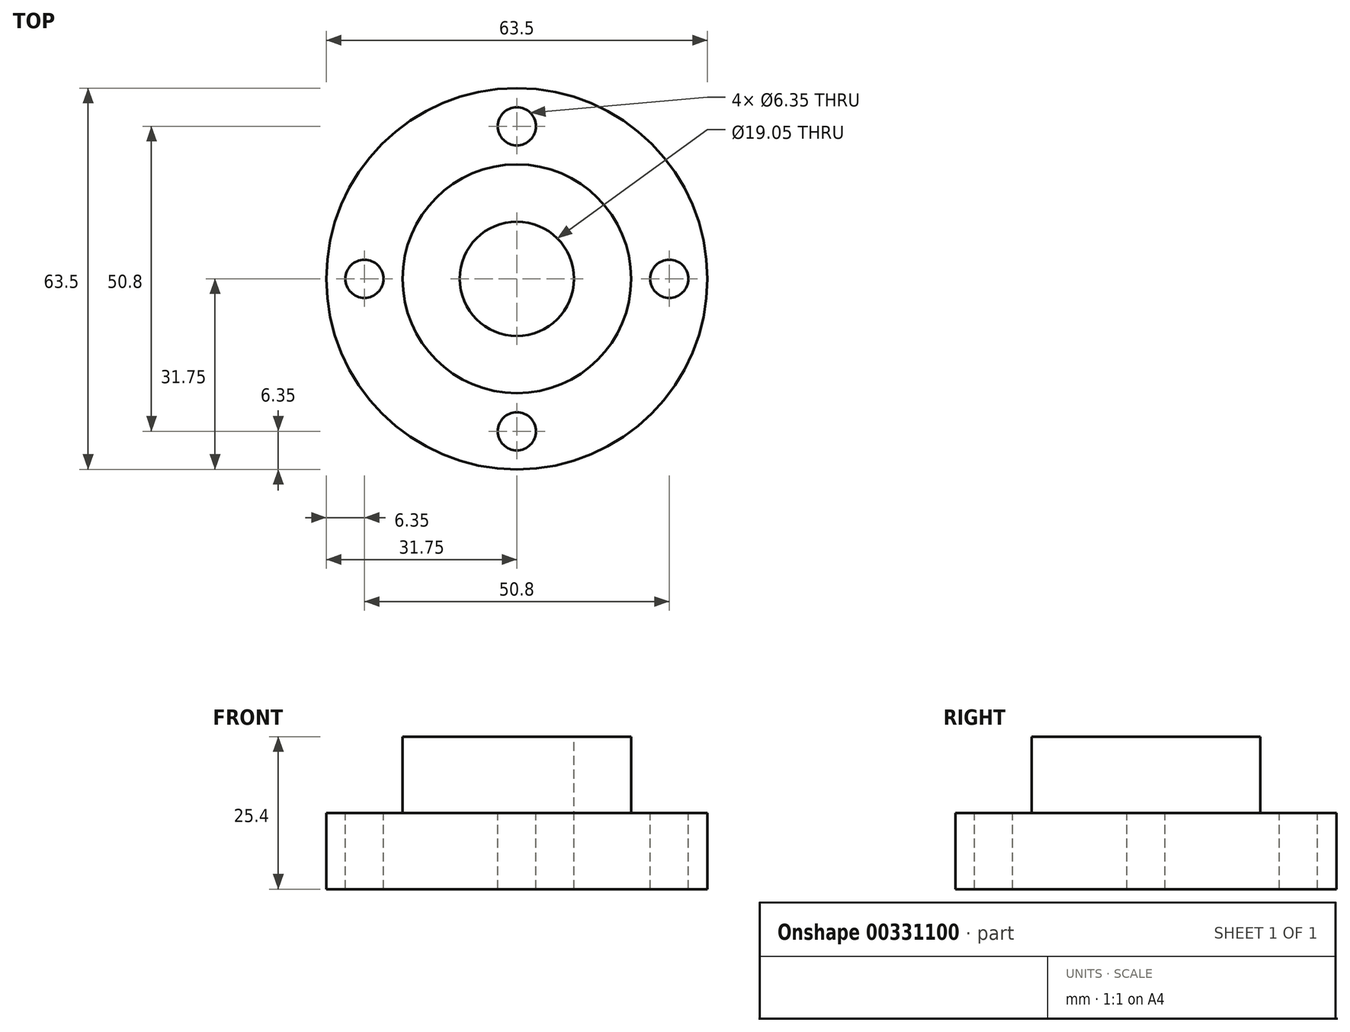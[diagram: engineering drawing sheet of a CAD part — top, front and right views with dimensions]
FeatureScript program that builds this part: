
annotation { "Feature Type Name" : "Feature", "Feature Type Description" : "" }
export const myFeature = defineFeature(function(context is Context, id is Id, definition is map)
    precondition{}
    {
        {
            var Q0;
            Q0=qCreatedBy(makeId("Top.planeOp"),FACE);
            var sketch = newSketch(context, id + "F0", { "sketchPlane" : qUnion([Q0])});
            skLineSegment(sketch, "E0", {"start": v(0, 0) * mm, "end": v(0, 63.5) * mm});
            skLineSegment(sketch, "E1", {"start": v(0, 63.5) * mm, "end": v(63.5, 63.5) * mm});
            skLineSegment(sketch, "E2", {"start": v(63.5, 63.5) * mm, "end": v(63.5, 0) * mm});
            skLineSegment(sketch, "E3", {"start": v(63.5, 0) * mm, "end": v(0, 0) * mm});
            skSolve(sketch);
        }
        {
            var Q0;
            Q0 = qSketchRegion(id + "F0", true);
            extrude(context, id + "F1", {"entities" : qUnion([Q0]), "depth" : 25.4 * mm});
        }
        {
            var Q0;
            Q0=makeQuery(id+"F1.opExtrude","CAP_FACE",FACE,{"disambiguationData":[OSD([sQuery(id+"F0.wireOp",EDGE,"E0"),sQuery(id+"F0.wireOp",EDGE,"E1"),sQuery(id+"F0.wireOp",EDGE,"E2"),sQuery(id+"F0.wireOp",EDGE,"E3")])],"isStart":false});
            var sketch = newSketch(context, id + "F2", { "sketchPlane" : qUnion([Q0])});
            skLineSegment(sketch, "E4", {"start": v(0, 63.5) * mm, "end": v(63.5, 63.5) * mm});
            skLineSegment(sketch, "E5", {"start": v(63.5, 63.5) * mm, "end": v(63.5, 0) * mm});
            skLineSegment(sketch, "E6", {"start": v(63.5, 0) * mm, "end": v(0, 0) * mm});
            skLineSegment(sketch, "E7", {"start": v(0, 0) * mm, "end": v(0, 63.5) * mm});
            skLineSegment(sketch, "E8", {"start": v(31.75, 50.8) * mm, "end": v(50.8, 50.8) * mm});
            skLineSegment(sketch, "E9", {"start": v(50.8, 50.8) * mm, "end": v(50.8, 31.75) * mm});
            skLineSegment(sketch, "E10", {"start": v(50.8, 31.75) * mm, "end": v(50.8, 12.7) * mm});
            skLineSegment(sketch, "E11", {"start": v(50.8, 12.7) * mm, "end": v(12.7, 12.7) * mm});
            skLineSegment(sketch, "E12", {"start": v(12.7, 12.7) * mm, "end": v(12.7, 50.8) * mm});
            skLineSegment(sketch, "E13", {"start": v(12.7, 50.8) * mm, "end": v(31.75, 50.8) * mm});
            skPoint(sketch, "E14.orphan", {"position": v(31.75, 31.75) * mm});
            skPoint(sketch, "E15.start.orphan", {"position": v(0, 31.75) * mm});
            skPoint(sketch, "E16.trimOffspring.end.orphan", {"position": v(63.5, 31.75) * mm});
            skSolve(sketch);
        }
        {
            var Q0;
            Q0=makeQuery(id+"F2.imprint","IMPRINT",FACE,{"disambiguationData":[TD([[makeQuery(id+"F2.imprint","IMPRINT",EDGE,{"derivedFrom":sQuery(id+"F2.wireOp",EDGE,"E4")}),-1.0]])]});
            extrude(context, id + "F3", {"entities" : qUnion([Q0]), "operationType" : NewBodyOperationType.REMOVE, "oppositeDirection" : true, "depth" : 12.7 * mm});
        }
        {
            var Q0;
            Q0=makeQuery(id+"F3.boolean.opBoolean","COPY",FACE,{"derivedFrom":makeQuery(id+"F3.opExtrude","CAP_FACE",FACE,{"disambiguationData":[OSD([sQuery(id+"F2.wireOp",EDGE,"E4"),sQuery(id+"F2.wireOp",EDGE,"E5"),sQuery(id+"F2.wireOp",EDGE,"E6"),sQuery(id+"F2.wireOp",EDGE,"E7"),sQuery(id+"F2.wireOp",EDGE,"E8"),sQuery(id+"F2.wireOp",EDGE,"E9"),sQuery(id+"F2.wireOp",EDGE,"E10"),sQuery(id+"F2.wireOp",EDGE,"E11"),sQuery(id+"F2.wireOp",EDGE,"E12"),sQuery(id+"F2.wireOp",EDGE,"E13")])],"isStart":false})});
            var sketch = newSketch(context, id + "F4", { "sketchPlane" : qUnion([Q0])});
            skLineSegment(sketch, "E17", {"start": v(0, 31.75) * mm, "end": v(6.35, 31.75) * mm});
            skLineSegment(sketch, "E18", {"start": v(6.35, 31.75) * mm, "end": v(31.75, 63.5) * mm});
            skLineSegment(sketch, "E19", {"start": v(31.75, 57.15) * mm, "end": v(31.75, 63.5) * mm});
            skLineSegment(sketch, "E20", {"start": v(63.5, 31.75) * mm, "end": v(57.15, 31.75) * mm});
            skPoint(sketch, "E20.endSnap0", {"position": v(63.5, 31.75) * mm});
            skLineSegment(sketch, "E21", {"start": v(57.15, 31.75) * mm, "end": v(31.75, 0) * mm});
            skLineSegment(sketch, "E22", {"start": v(31.75, 6.35) * mm, "end": v(31.75, 0) * mm});
            skCircle(sketch, "E23", {"center": v(31.75, 57.15) * mm, "radius": 3.18 * mm});
            skCircle(sketch, "E24", {"center": v(57.15, 31.75) * mm, "radius": 3.18 * mm});
            skCircle(sketch, "E25", {"center": v(31.75, 6.35) * mm, "radius": 3.18 * mm});
            skCircle(sketch, "E26", {"center": v(6.35, 31.75) * mm, "radius": 3.18 * mm});
            skSolve(sketch);
        }
        {
            var Q0;
            Q0 = qSketchRegion(id + "F4", true);
            extrude(context, id + "F5", {"entities" : qUnion([Q0]), "operationType" : NewBodyOperationType.REMOVE, "oppositeDirection" : true, "depth" : 25.4 * mm});
        }
        {
            var Q0;
            Q0=makeQuery(id+"F1.opExtrude","CAP_FACE",FACE,{"disambiguationData":[OSD([sQuery(id+"F0.wireOp",EDGE,"E0"),sQuery(id+"F0.wireOp",EDGE,"E1"),sQuery(id+"F0.wireOp",EDGE,"E2"),sQuery(id+"F0.wireOp",EDGE,"E3")])],"isStart":false});
            var sketch = newSketch(context, id + "F6", { "sketchPlane" : qUnion([Q0])});
            skLineSegment(sketch, "E27", {"start": v(31.75, 50.8) * mm, "end": v(31.75, 12.7) * mm});
            skCircle(sketch, "E28", {"center": v(31.75, 31.75) * mm, "radius": 9.53 * mm});
            skSolve(sketch);
        }
        {
            var Q0;
            Q0 = qSketchRegion(id + "F6", true);
            extrude(context, id + "F7", {"entities" : qUnion([Q0]), "operationType" : NewBodyOperationType.REMOVE, "oppositeDirection" : true, "depth" : 25.4 * mm});
        }
        {
            var Q0;
            Q0=makeQuery(id+"F1.opExtrude","SWEPT_EDGE",EDGE,{"disambiguationData":[OSD([sQuery(id+"F0.wireOp",EDGE,"E0"),sQuery(id+"F0.wireOp",EDGE,"E3")])]});
            var Q1;
            Q1=makeQuery(id+"F1.opExtrude","SWEPT_EDGE",EDGE,{"disambiguationData":[OSD([sQuery(id+"F0.wireOp",EDGE,"E2"),sQuery(id+"F0.wireOp",EDGE,"E3")])]});
            var Q2;
            Q2=makeQuery(id+"F1.opExtrude","SWEPT_EDGE",EDGE,{"disambiguationData":[OSD([sQuery(id+"F0.wireOp",EDGE,"E1"),sQuery(id+"F0.wireOp",EDGE,"E2")])]});
            var Q3;
            Q3=makeQuery(id+"F1.opExtrude","SWEPT_EDGE",EDGE,{"disambiguationData":[OSD([sQuery(id+"F0.wireOp",EDGE,"E0"),sQuery(id+"F0.wireOp",EDGE,"E1")])]});
            fillet(context, id + "F8", {"entities" : qUnion([Q0, Q1, Q2, Q3]), "radius" : 31.75 * mm, "tangentPropagation" : true, "allowEdgeOverflow" : false});
        }
        {
            var Q0;
            Q0=makeQuery(id+"F3.boolean.opBoolean","COPY",EDGE,{"derivedFrom":makeQuery(id+"F3.opExtrude","SWEPT_EDGE",EDGE,{"disambiguationData":[OSD([sQuery(id+"F2.wireOp",EDGE,"E11"),sQuery(id+"F2.wireOp",EDGE,"E12")])]})});
            var Q1;
            Q1=makeQuery(id+"F3.boolean.opBoolean","COPY",EDGE,{"derivedFrom":makeQuery(id+"F3.opExtrude","SWEPT_EDGE",EDGE,{"disambiguationData":[OSD([sQuery(id+"F2.wireOp",EDGE,"E10"),sQuery(id+"F2.wireOp",EDGE,"E11")])]})});
            var Q2;
            Q2=makeQuery(id+"F3.boolean.opBoolean","COPY",EDGE,{"derivedFrom":makeQuery(id+"F3.opExtrude","SWEPT_EDGE",EDGE,{"disambiguationData":[OSD([sQuery(id+"F2.wireOp",EDGE,"E12"),sQuery(id+"F2.wireOp",EDGE,"E13")])]})});
            var Q3;
            Q3=makeQuery(id+"F3.boolean.opBoolean","COPY",EDGE,{"derivedFrom":makeQuery(id+"F3.opExtrude","SWEPT_EDGE",EDGE,{"disambiguationData":[OSD([sQuery(id+"F2.wireOp",EDGE,"E8"),sQuery(id+"F2.wireOp",EDGE,"E9")])]})});
            fillet(context, id + "F9", {"entities" : qUnion([Q0, Q1, Q2, Q3]), "radius" : 19.05 * mm, "tangentPropagation" : true, "allowEdgeOverflow" : false});
        }
    });
